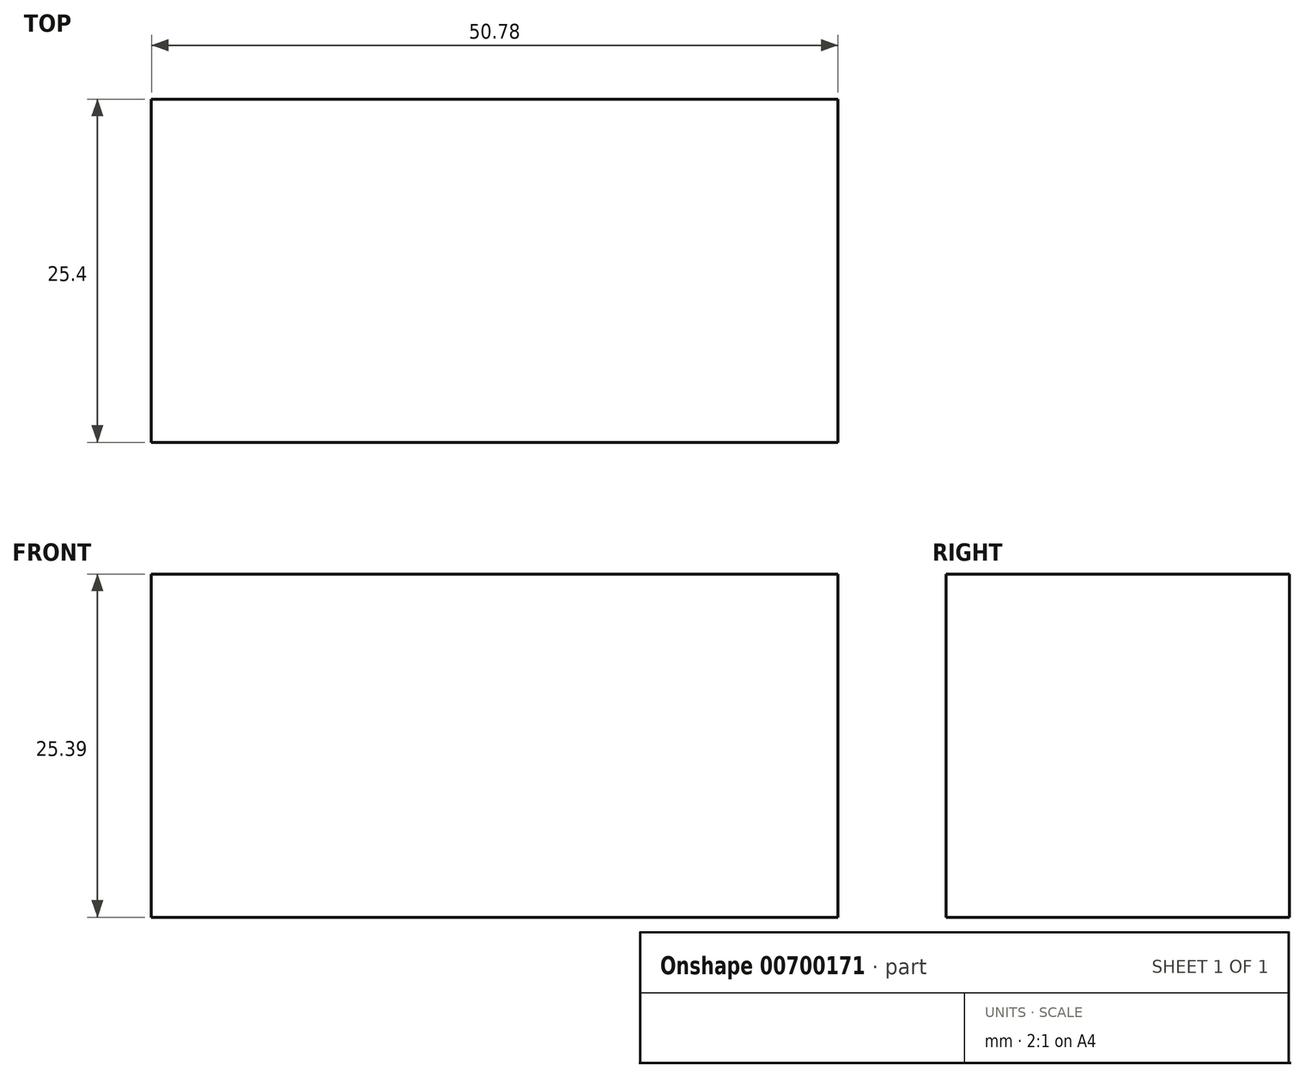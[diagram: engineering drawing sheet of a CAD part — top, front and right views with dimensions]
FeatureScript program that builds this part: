
annotation { "Feature Type Name" : "Feature", "Feature Type Description" : "" }
export const myFeature = defineFeature(function(context is Context, id is Id, definition is map)
    precondition{}
    {
        {
            var Q0;
            Q0=qCreatedBy(makeId("Front.planeOp"),FACE);
            var sketch = newSketch(context, id + "F0", { "sketchPlane" : qUnion([Q0])});
            skLineSegment(sketch, "E0.bottom", {"start": v(-27.86, -12.8) * mm, "end": v(22.92, -12.8) * mm});
            skLineSegment(sketch, "E0.top", {"start": v(-27.86, 12.59) * mm, "end": v(22.92, 12.59) * mm});
            skLineSegment(sketch, "E0.left", {"start": v(-27.86, -12.8) * mm, "end": v(-27.86, 12.59) * mm});
            skLineSegment(sketch, "E0.right", {"start": v(22.92, -12.8) * mm, "end": v(22.92, 12.59) * mm});
            skSolve(sketch);
        }
        {
            var Q0;
            Q0=makeQuery(id+"F0.imprint","IMPRINT",FACE,{"disambiguationData":[TD([[makeQuery(id+"F0.imprint","IMPRINT",EDGE,{"derivedFrom":sQuery(id+"F0.wireOp",EDGE,"E0.bottom")}),1.0]])]});
            extrude(context, id + "F1", {"entities" : qUnion([Q0]), "depth" : 25.4 * mm, "offsetDistance" : 25.4 * mm});
        }
    });
